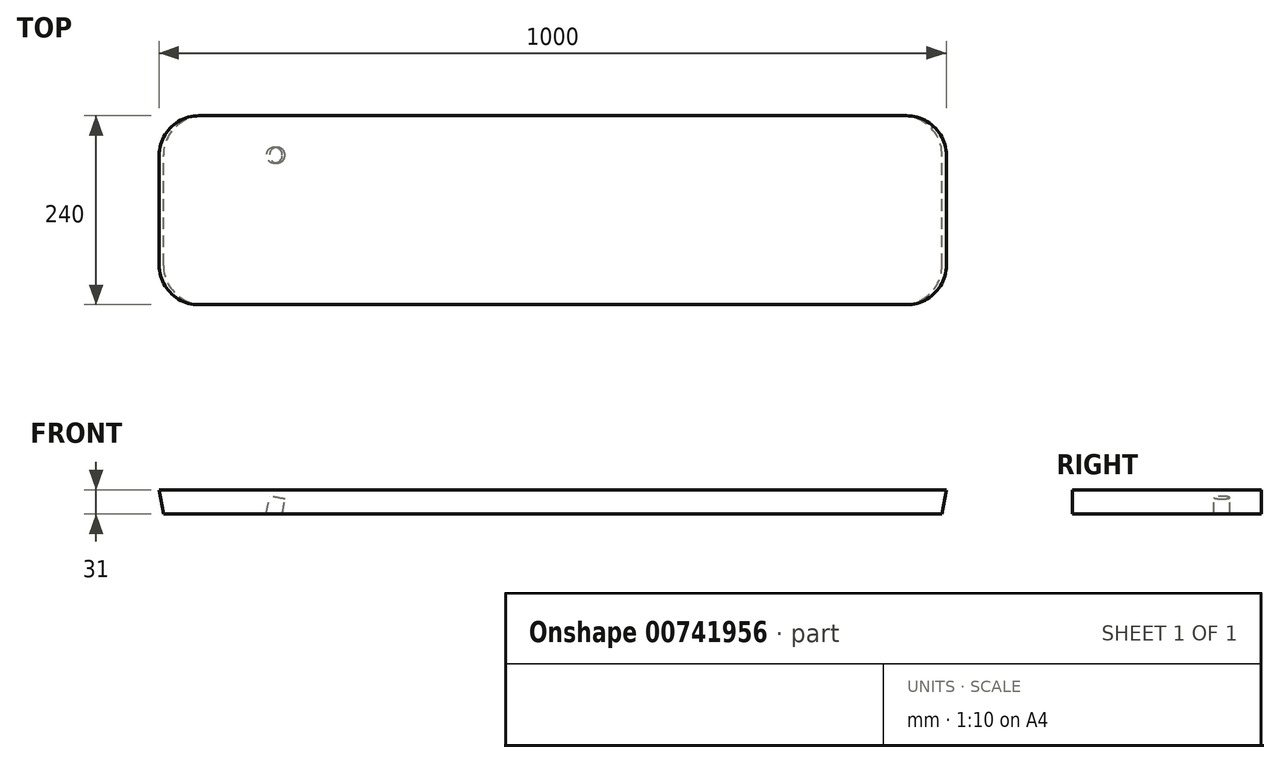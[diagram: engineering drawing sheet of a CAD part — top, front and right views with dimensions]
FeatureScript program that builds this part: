
annotation { "Feature Type Name" : "Feature", "Feature Type Description" : "" }
export const myFeature = defineFeature(function(context is Context, id is Id, definition is map)
    precondition{}
    {
        {
            var Q0;
            Q0=qCreatedBy(makeId("Front.planeOp"),FACE);
            var sketch = newSketch(context, id + "F0", { "sketchPlane" : qUnion([Q0])});
            skLineSegment(sketch, "E0", {"start": v(0, 74.58) * mm, "end": v(500, 74.58) * mm});
            skLineSegment(sketch, "E1", {"start": v(500, 74.58) * mm, "end": v(494.53, 43.58) * mm});
            skLineSegment(sketch, "E2", {"start": v(494.53, 43.58) * mm, "end": v(0, 43.58) * mm});
            skLineSegment(sketch, "E3.MirrorCS", {"start": v(0, 74.58) * mm, "end": v(-500, 74.58) * mm});
            skLineSegment(sketch, "E4.MirrorCS", {"start": v(-500, 74.58) * mm, "end": v(-494.53, 43.58) * mm});
            skLineSegment(sketch, "E5.MirrorCS", {"start": v(-494.53, 43.58) * mm, "end": v(0, 43.58) * mm});
            skSolve(sketch);
        }
        {
            var Q0;
            Q0 = qSketchRegion(id + "F0", true);
            extrude(context, id + "F1", {"entities" : qUnion([Q0]), "depth" : 120 * mm, "offsetDistance" : 25 * mm});
        }
        {
            var Q0;
            Q0=makeQuery(id+"F1.opExtrude","SWEPT_BODY",BODY,{"disambiguationData":[OSD([sQuery(id+"F0.wireOp",EDGE,"E0"),sQuery(id+"F0.wireOp",EDGE,"E1"),sQuery(id+"F0.wireOp",EDGE,"E2"),sQuery(id+"F0.wireOp",EDGE,"E3.MirrorCS"),sQuery(id+"F0.wireOp",EDGE,"E4.MirrorCS"),sQuery(id+"F0.wireOp",EDGE,"E5.MirrorCS")])]});
            var Q1;
            Q1=qCreatedBy(makeId("Front.planeOp"),FACE);
            mirror(context, id + "F2", {"operationType" : NewBodyOperationType.ADD, "entities" : qUnion([Q0]), "mirrorPlane" : qUnion([Q1])});
        }
        {
            var Q0;
            Q0=makeQuery(id+"F1.opExtrude","CAP_EDGE",EDGE,{"disambiguationData":[OSD([sQuery(id+"F0.wireOp",EDGE,"E1")])],"isStart":false});
            fillet(context, id + "F3", {"entities" : qUnion([Q0]), "radius" : 50 * mm, "tangentPropagation" : true, "allowEdgeOverflow" : false});
        }
        {
            var Q0;
            Q0=makeQuery(id+"F2.opPattern","COPY",EDGE,{"derivedFrom":makeQuery(id+"F1.opExtrude","CAP_EDGE",EDGE,{"disambiguationData":[OSD([sQuery(id+"F0.wireOp",EDGE,"E1")])],"isStart":false}),"instanceName":"1"});
            fillet(context, id + "F4", {"entities" : qUnion([Q0]), "radius" : 50 * mm, "tangentPropagation" : true, "allowEdgeOverflow" : false});
        }
        {
            var Q0;
            Q0=makeQuery(id+"F1.opExtrude","CAP_EDGE",EDGE,{"disambiguationData":[OSD([sQuery(id+"F0.wireOp",EDGE,"E4.MirrorCS")])],"isStart":false});
            fillet(context, id + "F5", {"entities" : qUnion([Q0]), "radius" : 50 * mm, "tangentPropagation" : true, "allowEdgeOverflow" : false});
        }
        {
            var Q0;
            Q0=makeQuery(id+"F2.opPattern","COPY",EDGE,{"derivedFrom":makeQuery(id+"F1.opExtrude","CAP_EDGE",EDGE,{"disambiguationData":[OSD([sQuery(id+"F0.wireOp",EDGE,"E4.MirrorCS")])],"isStart":false}),"instanceName":"1"});
            fillet(context, id + "F6", {"entities" : qUnion([Q0]), "radius" : 50 * mm, "tangentPropagation" : true, "allowEdgeOverflow" : false});
        }
        {
            var Q0;
            {var subQ0=makeQuery(id+"F1.opExtrude","SWEPT_FACE",FACE,{"disambiguationData":[OSD([sQuery(id+"F0.wireOp",EDGE,"E0"),sQuery(id+"F0.wireOp",EDGE,"E3.MirrorCS")])]});Q0=makeQuery(id+"F2.boolean.opBoolean","MERGE",FACE,{"derivedFrom":[subQ0,makeQuery(id+"F2.opPattern","COPY",FACE,{"derivedFrom":subQ0,"instanceName":"1"})]});}
            cPlane(context, id + "F7", {"entities" : qUnion([Q0]), "cplaneType" : CPlaneType.OFFSET, "offset" : 10 * mm, "oppositeDirection" : true, "width" : 150 * mm, "height" : 150 * mm});
        }
        {
            var Q0;
            Q0=qCreatedBy(id+"F7.planeOp",FACE);
            var sketch = newSketch(context, id + "F8", { "sketchPlane" : qUnion([Q0])});
            skLineSegment(sketch, "E6", {"start": v(-804.03, 0) * mm, "end": v(886.9, 0) * mm, "construction": true});
            skLineSegment(sketch, "E7", {"start": v(0, -336.29) * mm, "end": v(0, 302.6) * mm, "construction": true});
            skLineSegment(sketch, "E8", {"start": v(-350, 295.53) * mm, "end": v(-350, -357.9) * mm, "construction": true});
            skLineSegment(sketch, "E9.MirrorCS", {"start": v(350, 295.53) * mm, "end": v(350, -357.9) * mm, "construction": true});
            skLineSegment(sketch, "E10", {"start": v(-804.03, 70) * mm, "end": v(886.9, 70) * mm, "construction": true});
            skLineSegment(sketch, "E11.MirrorCS", {"start": v(-804.03, -70) * mm, "end": v(886.9, -70) * mm, "construction": true});
            skSolve(sketch);
        }
        {
            var Q0;
            Q0=sQuery(id+"F8.wireOp",EDGE,"E8");
            cPlane(context, id + "F9", {"entities" : qUnion([Q0]), "cplaneType" : CPlaneType.LINE_ANGLE, "offset" : 25 * mm, "angle" : 170 * degree, "width" : 150 * mm, "height" : 150 * mm});
        }
        {
            var Q0;
            Q0=qCreatedBy(id+"F9.planeOp",FACE);
            var sketch = newSketch(context, id + "F10", { "sketchPlane" : qUnion([Q0])});
            skCircle(sketch, "E12", {"center": v(-355.9, 70) * mm, "radius": 10 * mm});
            skSolve(sketch);
        }
        {
            var Q0;
            Q0 = qSketchRegion(id + "F10", true);
            var Q1;
            Q1=sQuery(id+"F10.wireOp",EDGE,"E12");
            extrude(context, id + "F11", {"entities" : qUnion([Q0]), "operationType" : NewBodyOperationType.REMOVE, "surfaceEntities" : qUnion([Q1]), "endBound" : BoundingType.THROUGH_ALL, "oppositeDirection" : true, "depth" : 25 * mm, "offsetDistance" : 25 * mm});
        }
    });
